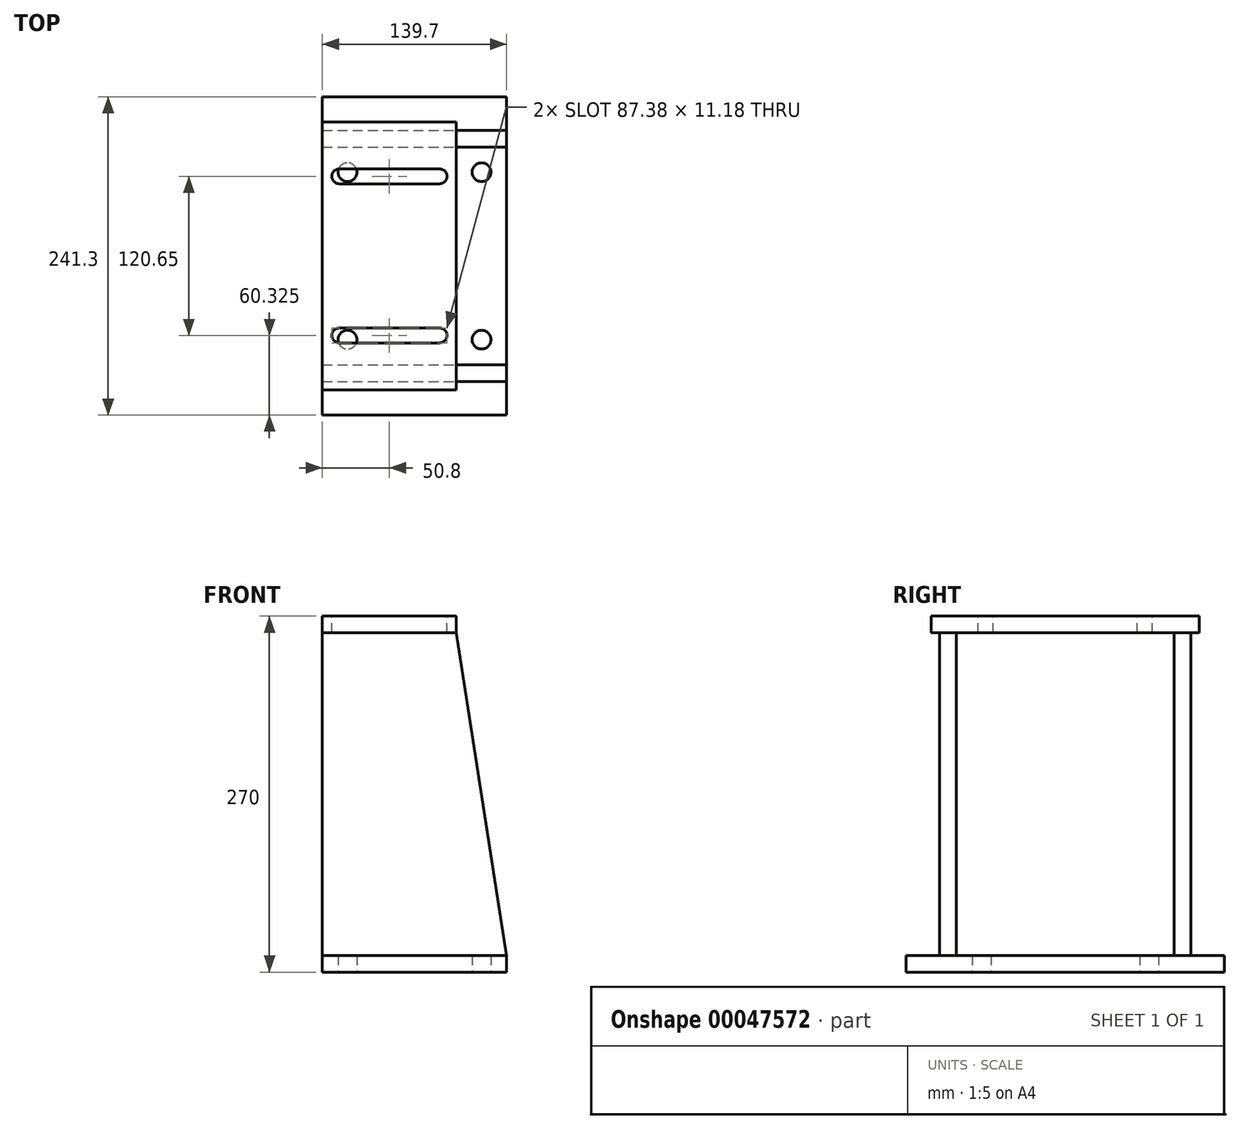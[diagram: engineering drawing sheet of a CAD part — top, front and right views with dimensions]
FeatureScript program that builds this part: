
annotation { "Feature Type Name" : "Feature", "Feature Type Description" : "" }
export const myFeature = defineFeature(function(context is Context, id is Id, definition is map)
    precondition{}
    {
        {
            var Q0;
            Q0=qCreatedBy(makeId("Top.planeOp"),FACE);
            var sketch = newSketch(context, id + "F0", { "sketchPlane" : qUnion([Q0])});
            skLineSegment(sketch, "E0.rect.bottom", {"start": v(-69.85, 120.65) * mm, "end": v(69.85, 120.65) * mm});
            skLineSegment(sketch, "E0.rect.top", {"start": v(-69.85, -120.65) * mm, "end": v(69.85, -120.65) * mm});
            skLineSegment(sketch, "E0.rect.left", {"start": v(-69.85, 120.65) * mm, "end": v(-69.85, -120.65) * mm});
            skLineSegment(sketch, "E0.rect.right", {"start": v(69.85, 120.65) * mm, "end": v(69.85, -120.65) * mm});
            skPoint(sketch, "E0.rect.middle", {"position": v(0, 0) * mm});
            skLineSegment(sketch, "E1", {"start": v(0, 120.65) * mm, "end": v(0, -120.65) * mm, "construction": true});
            skLineSegment(sketch, "E2", {"start": v(-69.85, 0) * mm, "end": v(69.85, 0) * mm, "construction": true});
            skLineSegment(sketch, "E3.0", {"start": v(-69.85, 63.5) * mm, "end": v(69.85, 63.5) * mm, "construction": true});
            skLineSegment(sketch, "E4.0", {"start": v(-50.8, 120.65) * mm, "end": v(-50.8, -120.65) * mm, "construction": true});
            skCircle(sketch, "E5", {"center": v(-50.8, 63.5) * mm, "radius": 7.14 * mm});
            skCircle(sketch, "E6.MirrorC", {"center": v(50.8, 63.5) * mm, "radius": 7.14 * mm});
            skCircle(sketch, "E7.MirrorC", {"center": v(-50.8, -63.5) * mm, "radius": 7.14 * mm});
            skCircle(sketch, "E8.MirrorC", {"center": v(50.8, -63.5) * mm, "radius": 7.14 * mm});
            skSolve(sketch);
        }
        {
            var Q0;
            Q0 = qSketchRegion(id + "F0", true);
            extrude(context, id + "F1", {"entities" : qUnion([Q0]), "depth" : 12.7 * mm});
        }
        {
            var Q0;
            Q0=qCreatedBy(makeId("Top.planeOp"),FACE);
            cPlane(context, id + "F2", {"entities" : qUnion([Q0]), "cplaneType" : CPlaneType.OFFSET, "offset" : 270 * mm, "width" : 152.4 * mm, "height" : 152.4 * mm});
        }
        {
            var Q0;
            Q0=qCreatedBy(id+"F2.planeOp",FACE);
            var sketch = newSketch(context, id + "F3", { "sketchPlane" : qUnion([Q0])});
            skLineSegment(sketch, "E9.0", {"start": v(-69.85, 120.65) * mm, "end": v(-69.85, -120.65) * mm, "construction": true});
            skLineSegment(sketch, "E10", {"start": v(-85.57, 0) * mm, "end": v(91.78, 0) * mm, "construction": true});
            skLineSegment(sketch, "E11.bottom", {"start": v(-69.85, 101.6) * mm, "end": v(31.75, 101.6) * mm});
            skLineSegment(sketch, "E11.top", {"start": v(-69.85, -101.6) * mm, "end": v(31.75, -101.6) * mm});
            skLineSegment(sketch, "E11.left", {"start": v(-69.85, 101.6) * mm, "end": v(-69.85, -101.6) * mm});
            skLineSegment(sketch, "E11.right", {"start": v(31.75, 101.6) * mm, "end": v(31.75, -101.6) * mm});
            skLineSegment(sketch, "E12.0", {"start": v(-85.57, 60.33) * mm, "end": v(91.78, 60.33) * mm, "construction": true});
            skLineSegment(sketch, "E13", {"start": v(-19.05, 101.6) * mm, "end": v(-19.05, -101.6) * mm, "construction": true});
            skLineSegment(sketch, "E14.0", {"start": v(-57.15, 101.6) * mm, "end": v(-57.15, -101.6) * mm, "construction": true});
            skLineSegment(sketch, "E15.MirrorCS", {"start": v(19.05, 101.6) * mm, "end": v(19.05, -101.6) * mm, "construction": true});
            skLineSegment(sketch, "E16", {"start": v(-57.15, 60.33) * mm, "end": v(19.05, 60.33) * mm});
            skArc(sketch, "E17.0.startCap", {"start": v(-57.15, 54.74) * mm, "mid": v(-62.74, 60.33) * mm, "end": v(-57.15, 65.91) * mm});
            skArc(sketch, "E17.0.endCap", {"start": v(19.05, 65.91) * mm, "mid": v(24.64, 60.33) * mm, "end": v(19.05, 54.74) * mm});
            skLineSegment(sketch, "E17.0.left", {"start": v(-57.15, 65.91) * mm, "end": v(19.05, 65.91) * mm});
            skLineSegment(sketch, "E17.0.right", {"start": v(-57.15, 54.74) * mm, "end": v(19.05, 54.74) * mm});
            skLineSegment(sketch, "E18.MirrorCS", {"start": v(-57.15, -54.74) * mm, "end": v(19.05, -54.74) * mm});
            skLineSegment(sketch, "E19.MirrorCS", {"start": v(-57.15, -65.91) * mm, "end": v(19.05, -65.91) * mm});
            skArc(sketch, "E20.MirrorCS", {"start": v(19.05, -65.91) * mm, "mid": v(24.64, -60.33) * mm, "end": v(19.05, -54.74) * mm});
            skArc(sketch, "E21.MirrorCS", {"start": v(-57.15, -54.74) * mm, "mid": v(-62.74, -60.33) * mm, "end": v(-57.15, -65.91) * mm});
            skLineSegment(sketch, "E22.MirrorCS", {"start": v(-57.15, -60.33) * mm, "end": v(19.05, -60.33) * mm});
            skSolve(sketch);
        }
        {
            var Q0;
            Q0 = qSketchRegion(id + "F3", true);
            extrude(context, id + "F4", {"entities" : qUnion([Q0]), "oppositeDirection" : true, "depth" : 12.7 * mm});
        }
        {
            var Q0;
            Q0=makeQuery(id+"F1.opExtrude","CAP_FACE",FACE,{"disambiguationData":[OSD([sQuery(id+"F0.wireOp",EDGE,"E0.rect.bottom"),sQuery(id+"F0.wireOp",EDGE,"E0.rect.top"),sQuery(id+"F0.wireOp",EDGE,"E0.rect.left"),sQuery(id+"F0.wireOp",EDGE,"E0.rect.right"),sQuery(id+"F0.wireOp",EDGE,"E5"),sQuery(id+"F0.wireOp",EDGE,"E6.MirrorC"),sQuery(id+"F0.wireOp",EDGE,"E7.MirrorC"),sQuery(id+"F0.wireOp",EDGE,"E8.MirrorC")])],"isStart":false});
            var sketch = newSketch(context, id + "F5", { "sketchPlane" : qUnion([Q0])});
            skLineSegment(sketch, "E23.0", {"start": v(-69.85, 95.25) * mm, "end": v(69.85, 95.25) * mm});
            skLineSegment(sketch, "E24.0", {"start": v(-69.85, 82.55) * mm, "end": v(69.85, 82.55) * mm});
            skLineSegment(sketch, "E25.0", {"start": v(69.85, 95.25) * mm, "end": v(69.85, 82.55) * mm});
            skLineSegment(sketch, "E26.0", {"start": v(-69.85, 95.25) * mm, "end": v(-69.85, 82.55) * mm});
            skPoint(sketch, "E27.orphan", {"position": v(-69.85, 120.65) * mm});
            skPoint(sketch, "E28.orphan", {"position": v(-69.85, -120.65) * mm});
            skPoint(sketch, "E29.orphan", {"position": v(69.85, 120.65) * mm});
            skPoint(sketch, "E30.orphan", {"position": v(69.85, -120.65) * mm});
            skLineSegment(sketch, "E31", {"start": v(-90.75, 0) * mm, "end": v(99.61, 0) * mm, "construction": true});
            skPoint(sketch, "E31.endSnap0", {"position": v(69.85, 0) * mm});
            skLineSegment(sketch, "E32.MirrorCS", {"start": v(-69.85, -95.25) * mm, "end": v(-69.85, -82.55) * mm});
            skLineSegment(sketch, "E33.MirrorCS", {"start": v(69.85, -95.25) * mm, "end": v(69.85, -82.55) * mm});
            skLineSegment(sketch, "E34.MirrorCS", {"start": v(-69.85, -95.25) * mm, "end": v(69.85, -95.25) * mm});
            skLineSegment(sketch, "E35.MirrorCS", {"start": v(-69.85, -82.55) * mm, "end": v(69.85, -82.55) * mm});
            skSolve(sketch);
        }
        {
            var Q0;
            Q0 = qSketchRegion(id + "F5", true);
            var Q1;
            Q1=makeQuery(id+"F4.opExtrude","CAP_FACE",FACE,{"disambiguationData":[OSD([sQuery(id+"F3.wireOp",EDGE,"E11.bottom"),sQuery(id+"F3.wireOp",EDGE,"E11.top"),sQuery(id+"F3.wireOp",EDGE,"E11.left"),sQuery(id+"F3.wireOp",EDGE,"E11.right"),sQuery(id+"F3.wireOp",EDGE,"E17.0.startCap"),sQuery(id+"F3.wireOp",EDGE,"E17.0.endCap"),sQuery(id+"F3.wireOp",EDGE,"E17.0.left"),sQuery(id+"F3.wireOp",EDGE,"E17.0.right"),sQuery(id+"F3.wireOp",EDGE,"E18.MirrorCS"),sQuery(id+"F3.wireOp",EDGE,"E19.MirrorCS"),sQuery(id+"F3.wireOp",EDGE,"E20.MirrorCS"),sQuery(id+"F3.wireOp",EDGE,"E21.MirrorCS")])],"isStart":false});
            extrude(context, id + "F6", {"entities" : qUnion([Q0]), "endBound" : BoundingType.UP_TO_SURFACE, "endBoundEntityFace" : qUnion([Q1]), "depth" : 25.4 * mm});
        }
        {
            var Q0;
            Q0=makeQuery(id+"F1.opExtrude","SWEPT_BODY",BODY,{"disambiguationData":[OSD([sQuery(id+"F0.wireOp",EDGE,"E0.rect.bottom"),sQuery(id+"F0.wireOp",EDGE,"E0.rect.top"),sQuery(id+"F0.wireOp",EDGE,"E0.rect.left"),sQuery(id+"F0.wireOp",EDGE,"E0.rect.right"),sQuery(id+"F0.wireOp",EDGE,"E5"),sQuery(id+"F0.wireOp",EDGE,"E6.MirrorC"),sQuery(id+"F0.wireOp",EDGE,"E7.MirrorC"),sQuery(id+"F0.wireOp",EDGE,"E8.MirrorC")])]});
            var Q1;
            Q1=makeQuery(id+"F6.opExtrude","SWEPT_BODY",BODY,{"disambiguationData":[OSD([sQuery(id+"F5.wireOp",EDGE,"E32.MirrorCS"),sQuery(id+"F5.wireOp",EDGE,"E33.MirrorCS"),sQuery(id+"F5.wireOp",EDGE,"E34.MirrorCS"),sQuery(id+"F5.wireOp",EDGE,"E35.MirrorCS")])]});
            var Q2;
            Q2=makeQuery(id+"F6.opExtrude","SWEPT_BODY",BODY,{"disambiguationData":[OSD([sQuery(id+"F5.wireOp",EDGE,"E23.0"),sQuery(id+"F5.wireOp",EDGE,"E24.0"),sQuery(id+"F5.wireOp",EDGE,"E25.0"),sQuery(id+"F5.wireOp",EDGE,"E26.0")])]});
            var Q3;
            Q3=makeQuery(id+"F4.opExtrude","SWEPT_BODY",BODY,{"disambiguationData":[OSD([sQuery(id+"F3.wireOp",EDGE,"E11.bottom"),sQuery(id+"F3.wireOp",EDGE,"E11.top"),sQuery(id+"F3.wireOp",EDGE,"E11.left"),sQuery(id+"F3.wireOp",EDGE,"E11.right"),sQuery(id+"F3.wireOp",EDGE,"E17.0.startCap"),sQuery(id+"F3.wireOp",EDGE,"E17.0.endCap"),sQuery(id+"F3.wireOp",EDGE,"E17.0.left"),sQuery(id+"F3.wireOp",EDGE,"E17.0.right"),sQuery(id+"F3.wireOp",EDGE,"E18.MirrorCS"),sQuery(id+"F3.wireOp",EDGE,"E19.MirrorCS"),sQuery(id+"F3.wireOp",EDGE,"E20.MirrorCS"),sQuery(id+"F3.wireOp",EDGE,"E21.MirrorCS")])]});
            booleanBodies(context, id + "F7", {"operationType" : BooleanOperationType.UNION, "tools" : qUnion([Q0, Q1, Q2, Q3])});
        }
        {
            var Q0;
            Q0=makeQuery(id+"F6.opExtrude","SWEPT_FACE",FACE,{"disambiguationData":[OSD([sQuery(id+"F5.wireOp",EDGE,"E34.MirrorCS")])]});
            var sketch = newSketch(context, id + "F8", { "sketchPlane" : qUnion([Q0])});
            skLineSegment(sketch, "E36.0", {"start": v(-69.85, 257.3) * mm, "end": v(31.75, 257.3) * mm, "construction": true});
            skLineSegment(sketch, "E37.0", {"start": v(31.75, 257.3) * mm, "end": v(31.75, 270) * mm, "construction": true});
            skLineSegment(sketch, "E38.0", {"start": v(-69.85, 12.7) * mm, "end": v(69.85, 12.7) * mm, "construction": true});
            skLineSegment(sketch, "E39.bottom", {"start": v(31.75, 257.3) * mm, "end": v(69.85, 257.3) * mm});
            skLineSegment(sketch, "E39.right", {"start": v(69.85, 257.3) * mm, "end": v(69.85, 12.7) * mm});
            skLineSegment(sketch, "E40", {"start": v(31.75, 257.3) * mm, "end": v(69.85, 12.7) * mm});
            skSolve(sketch);
        }
        {
            var Q0;
            Q0 = qSketchRegion(id + "F8", true);
            extrude(context, id + "F9", {"entities" : qUnion([Q0]), "operationType" : NewBodyOperationType.REMOVE, "endBound" : BoundingType.THROUGH_ALL, "oppositeDirection" : true, "depth" : 25.4 * mm});
        }
    });
